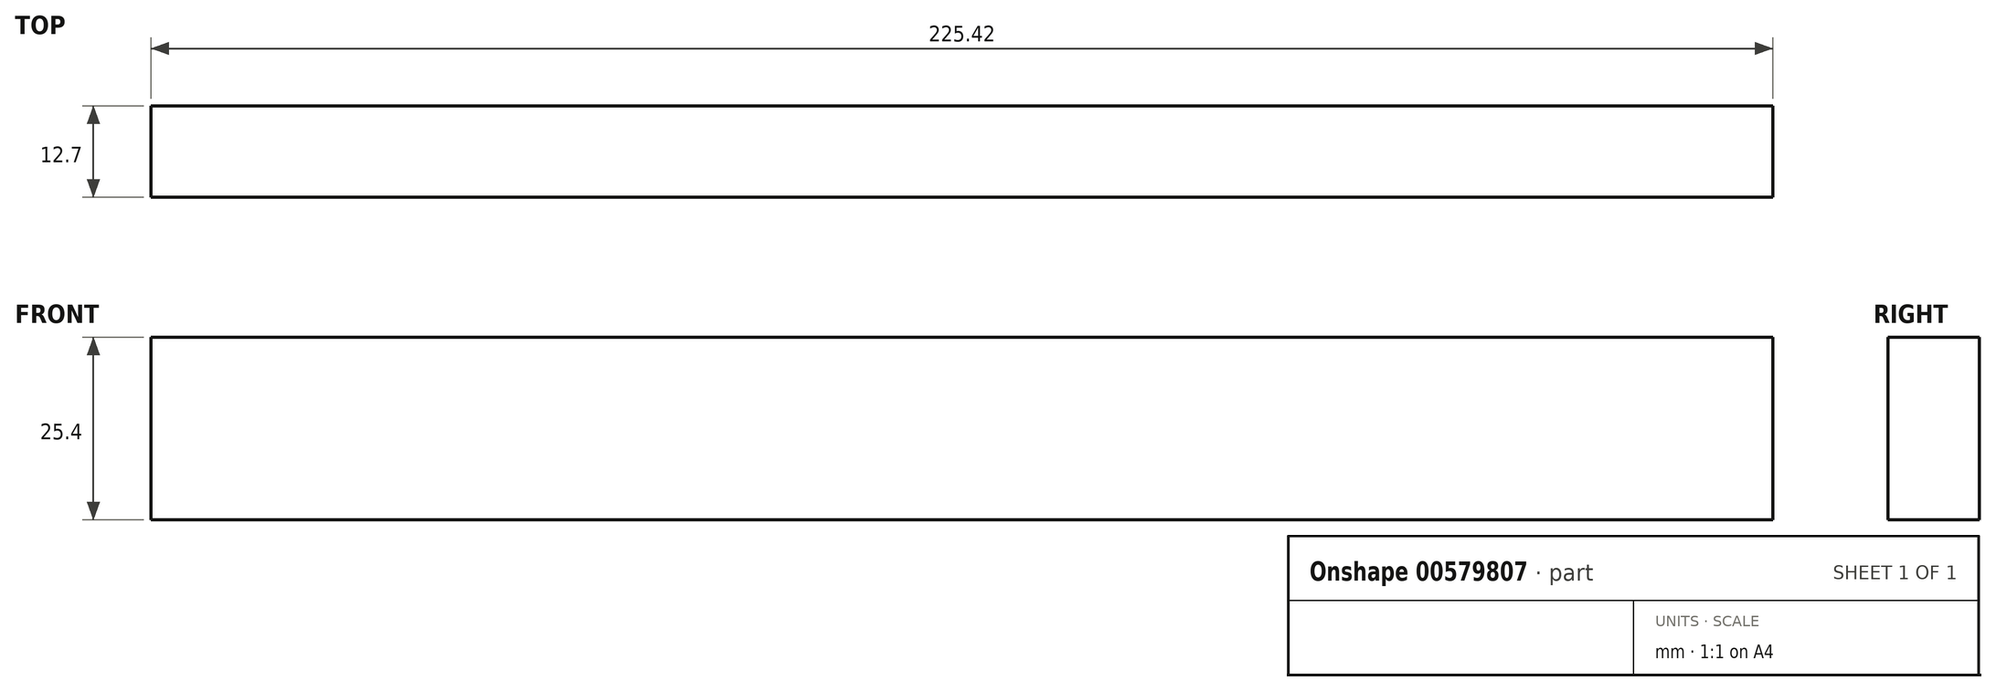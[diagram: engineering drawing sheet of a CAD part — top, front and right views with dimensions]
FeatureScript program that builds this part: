
annotation { "Feature Type Name" : "Feature", "Feature Type Description" : "" }
export const myFeature = defineFeature(function(context is Context, id is Id, definition is map)
    precondition{}
    {
        {
            var Q0;
            Q0=qCreatedBy(makeId("Right.planeOp"),FACE);
            var sketch = newSketch(context, id + "F0", { "sketchPlane" : qUnion([Q0])});
            skLineSegment(sketch, "E0.bottom", {"start": v(6.35, 12.7) * mm, "end": v(-6.35, 12.7) * mm});
            skLineSegment(sketch, "E0.top", {"start": v(6.35, -12.7) * mm, "end": v(-6.35, -12.7) * mm});
            skLineSegment(sketch, "E0.left", {"start": v(6.35, 12.7) * mm, "end": v(6.35, -12.7) * mm});
            skLineSegment(sketch, "E0.right", {"start": v(-6.35, 12.7) * mm, "end": v(-6.35, -12.7) * mm});
            skPoint(sketch, "E0.middle", {"position": v(0, 0) * mm});
            skSolve(sketch);
        }
        {
            var Q0;
            Q0=qSketchRegion(id+"F0",true);
            extrude(context, id + "F1", {"entities" : qUnion([Q0]), "depth" : 225.42 * mm, "offsetDistance" : 25.4 * mm});
        }
    });
